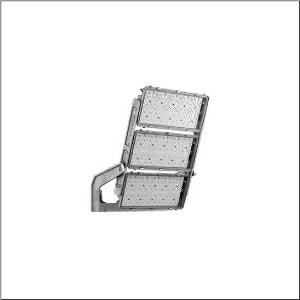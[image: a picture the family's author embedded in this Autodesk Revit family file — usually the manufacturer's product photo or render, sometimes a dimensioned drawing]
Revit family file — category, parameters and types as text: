
# Revit family: floodlight_fl_11_maxi_pro_remote___pl64blc_5xa779426w01aa_c02a
name_source: partatom
category: Lighting Fixtures
units: mm (PartAtom-declared; Revit-internal decimal feet)

## family parameters
Cut with Voids When Loaded = No
Host = Face
Light Source = No
Part Type = Normal
Room Calculation Point = No
Round Connector Dimension = Use Diameter
Shared = No

## types (1)
- --- (1 x LED, 140990 lm, 1516.9 W, 4000K)
    Apparent Load = 1517 VA
    CIE Flux Codes = 28 83 99 100 100
    Color Rendering = 70
    Color Temperature = 4000K
    Default Elevation = 1800 mm
    Description = Floodlight FL 11  maxi  pro Remote floodlight; light control with lens of PMMA; cover panel of toughened safety glass, transparent; light distribution: PL64BLC, asymmetric direct distribution, LEDcolour temperature: 4000K, rated luminous flux: 140.990lm, colour rendering: CRI > 70, light colour: 740; luminous efficacy: 93lm/W; brightness control: DALI 2 (1 DALI address); with terminal, 8-pole, max. 2.5mm², mains connection: 220..240V/380..400V AC, 50/60Hz, surge voltage resistance: line to ground: 10kV, ECG replaceable separately, no afterglow with DALI off / DMX off command, LED unit replaceable without ESD environment, dustproof LED module, dimming range 10..100%; 1517W floodlight with 2x LED unit of diecast aluminium, coated grey; length: 713mm / width: 651mm / height: 338mm; mounting bracket, of diecast aluminium, uncoated, natural, equipment: Power, protection rating (complete): IP66; insulation class (complete): insulation class I (protective earthing); certification: CE, ENEC, VDE; ball protection: ball impact resistance with accessories, impact resistance: IK07; only for outdoor installations, rated ambient temperature 10°C, permissible operating ambient temperature: -40..+30°C, permissible storage temperature: -40..+85°Cpackaging unit: 1 piece

Light Distribution: PL64BLC
    Height = 320 mm
    Lamp = 1 x LED
    Lamp Light Flux = 140990 lm
    Lamp Power = 1516.9 W
    Lamp count = 1
    Length = 1002 mm
    Luminous efficacy = 93 lm/W
    Manufacturer = Siteco
    ModVariant = No
    Model = 5XA779426W01AA
    Mounting Place = Ceiling
    Mounting Type = Surface mounted
    Number of Poles = 1
    OnlyDefault = Yes
    Power Factor = 1
    Product Name = Floodlight FL 11 maxi pro Remote | PL64BLC
    Product group = floodlight | ceiling mounted
    ProductGroupID = 301
    Protection Class = Protection class I
    Protection Degree = IP 66
    RLX_Detail_Level = 1
    RLX_Emergency_Light_Flux = 0 lm
    RLX_Emergency_Type = 0
    RLX_Emergency_Type_DB = No
    RlxData = <blob elided: 52605 chars, md5=ac38e361>
    Socket = socket
    Standby Power = 0 W
    System Light Flux = 140990 lm
    System Power = 1517 W
    Type Comments = factory setting: luminous flux: 100 % | dim-lin: 254 | 1070 mA
    Type Image = l_1349141.jpg
    URL = http://relux.com
    VarID = @adj_080904
    Voltage = 0 V
    Weight = 0.00 kg
    Width = 655 mm

## geometry (parser evidence)
native form markers: Blend x4, Sweep x13
no freeform markers — native parametric forms only
